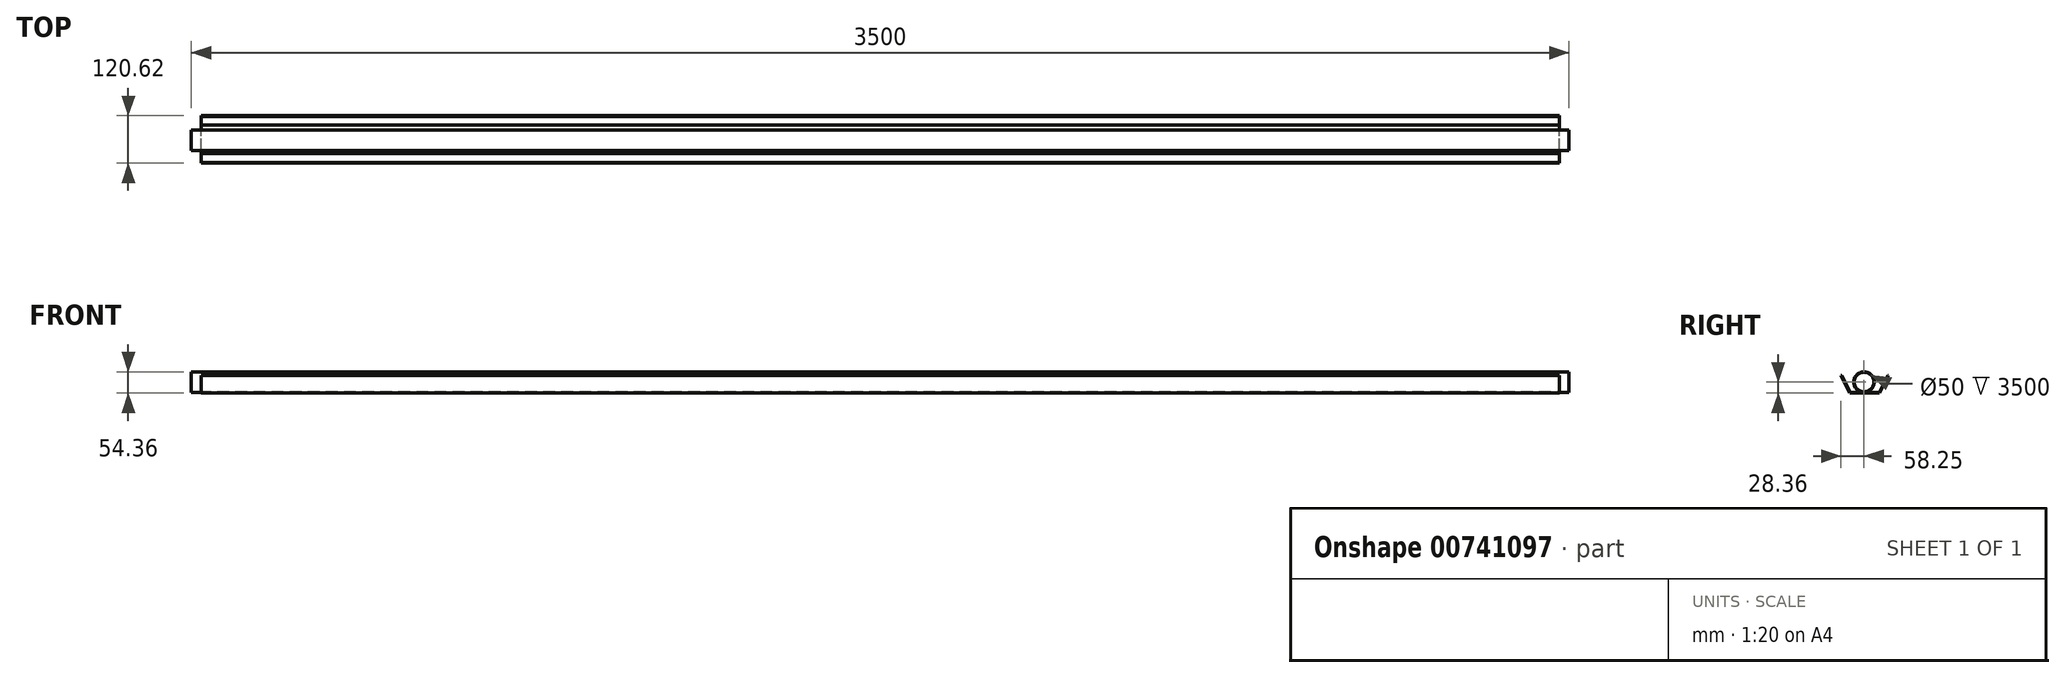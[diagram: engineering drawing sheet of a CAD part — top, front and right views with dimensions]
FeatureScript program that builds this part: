
annotation { "Feature Type Name" : "Feature", "Feature Type Description" : "" }
export const myFeature = defineFeature(function(context is Context, id is Id, definition is map)
    precondition{}
    {
        {
            var Q0;
            Q0=qCreatedBy(makeId("Right.planeOp"),FACE);
            var sketch = newSketch(context, id + "F0", { "sketchPlane" : qUnion([Q0])});
            skLineSegment(sketch, "E0", {"start": v(-35.44, -28.36) * mm, "end": v(39.56, -28.36) * mm});
            skLineSegment(sketch, "E1", {"start": v(-35.44, -28.36) * mm, "end": v(-58.25, 16.14) * mm});
            skLineSegment(sketch, "E2", {"start": v(-58.25, 16.14) * mm, "end": v(-56, 16.14) * mm});
            skLineSegment(sketch, "E3", {"start": v(62.37, 16.14) * mm, "end": v(39.56, -28.36) * mm});
            skLineSegment(sketch, "E4.0", {"start": v(-34.22, -26.36) * mm, "end": v(38.34, -26.36) * mm});
            skLineSegment(sketch, "E4.1", {"start": v(-34.22, -26.36) * mm, "end": v(-56, 16.14) * mm});
            skLineSegment(sketch, "E4.3", {"start": v(60.12, 16.14) * mm, "end": v(38.34, -26.36) * mm});
            skLineSegment(sketch, "E5.trimOffspring", {"start": v(60.12, 16.14) * mm, "end": v(62.37, 16.14) * mm});
            skSolve(sketch);
        }
        {
            var Q0;
            Q0=makeQuery(id+"F0.imprint","IMPRINT",FACE,{"disambiguationData":[TD([[makeQuery(id+"F0.imprint","IMPRINT",EDGE,{"derivedFrom":sQuery(id+"F0.wireOp",EDGE,"E0")}),1.0]])]});
            extrude(context, id + "F1", {"entities" : qUnion([Q0]), "endBound" : BoundingType.SYMMETRIC, "depth" : 3450 * mm, "offsetDistance" : 25 * mm});
        }
        {
            var Q0;
            Q0=qCreatedBy(makeId("Right.planeOp"),FACE);
            var sketch = newSketch(context, id + "F2", { "sketchPlane" : qUnion([Q0])});
            skCircle(sketch, "E6", {"center": v(0, 0) * mm, "radius": 26 * mm});
            skCircle(sketch, "E7", {"center": v(0, 0) * mm, "radius": 25 * mm});
            skSolve(sketch);
        }
        {
            var Q0;
            Q0 = qSketchRegion(id + "F2", true);
            extrude(context, id + "F3", {"entities" : qUnion([Q0]), "endBound" : BoundingType.SYMMETRIC, "depth" : 3500 * mm, "offsetDistance" : 25 * mm});
        }
    });
